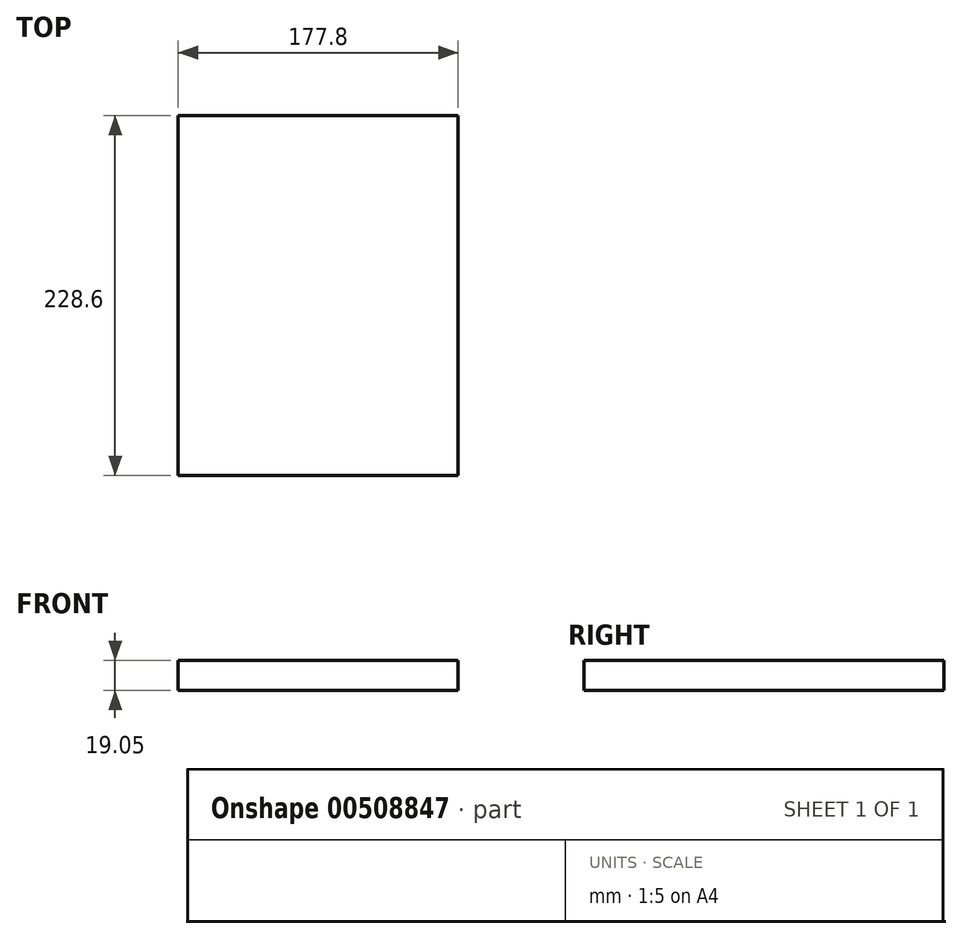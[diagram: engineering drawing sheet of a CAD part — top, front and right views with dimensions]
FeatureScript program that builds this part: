
annotation { "Feature Type Name" : "Feature", "Feature Type Description" : "" }
export const myFeature = defineFeature(function(context is Context, id is Id, definition is map)
    precondition{}
    {
        {
            var Q0;
            Q0=qCreatedBy(makeId("Top.planeOp"),FACE);
            var sketch = newSketch(context, id + "F0", { "sketchPlane" : qUnion([Q0])});
            skLineSegment(sketch, "E0.bottom", {"start": v(88.9, -114.3) * mm, "end": v(-88.9, -114.3) * mm});
            skLineSegment(sketch, "E0.top", {"start": v(88.9, 114.3) * mm, "end": v(-88.9, 114.3) * mm});
            skLineSegment(sketch, "E0.left", {"start": v(88.9, -114.3) * mm, "end": v(88.9, 114.3) * mm});
            skLineSegment(sketch, "E0.right", {"start": v(-88.9, -114.3) * mm, "end": v(-88.9, 114.3) * mm});
            skPoint(sketch, "E0.middle", {"position": v(0, 0) * mm});
            skSolve(sketch);
        }
        {
            var Q0;
            Q0=makeQuery(id+"F0.imprint","IMPRINT",FACE,{"disambiguationData":[TD([[makeQuery(id+"F0.imprint","IMPRINT",EDGE,{"derivedFrom":sQuery(id+"F0.wireOp",EDGE,"E0.bottom")}),-1.0]])]});
            extrude(context, id + "F1", {"entities" : qUnion([Q0]), "depth" : 19.05 * mm});
        }
    });
